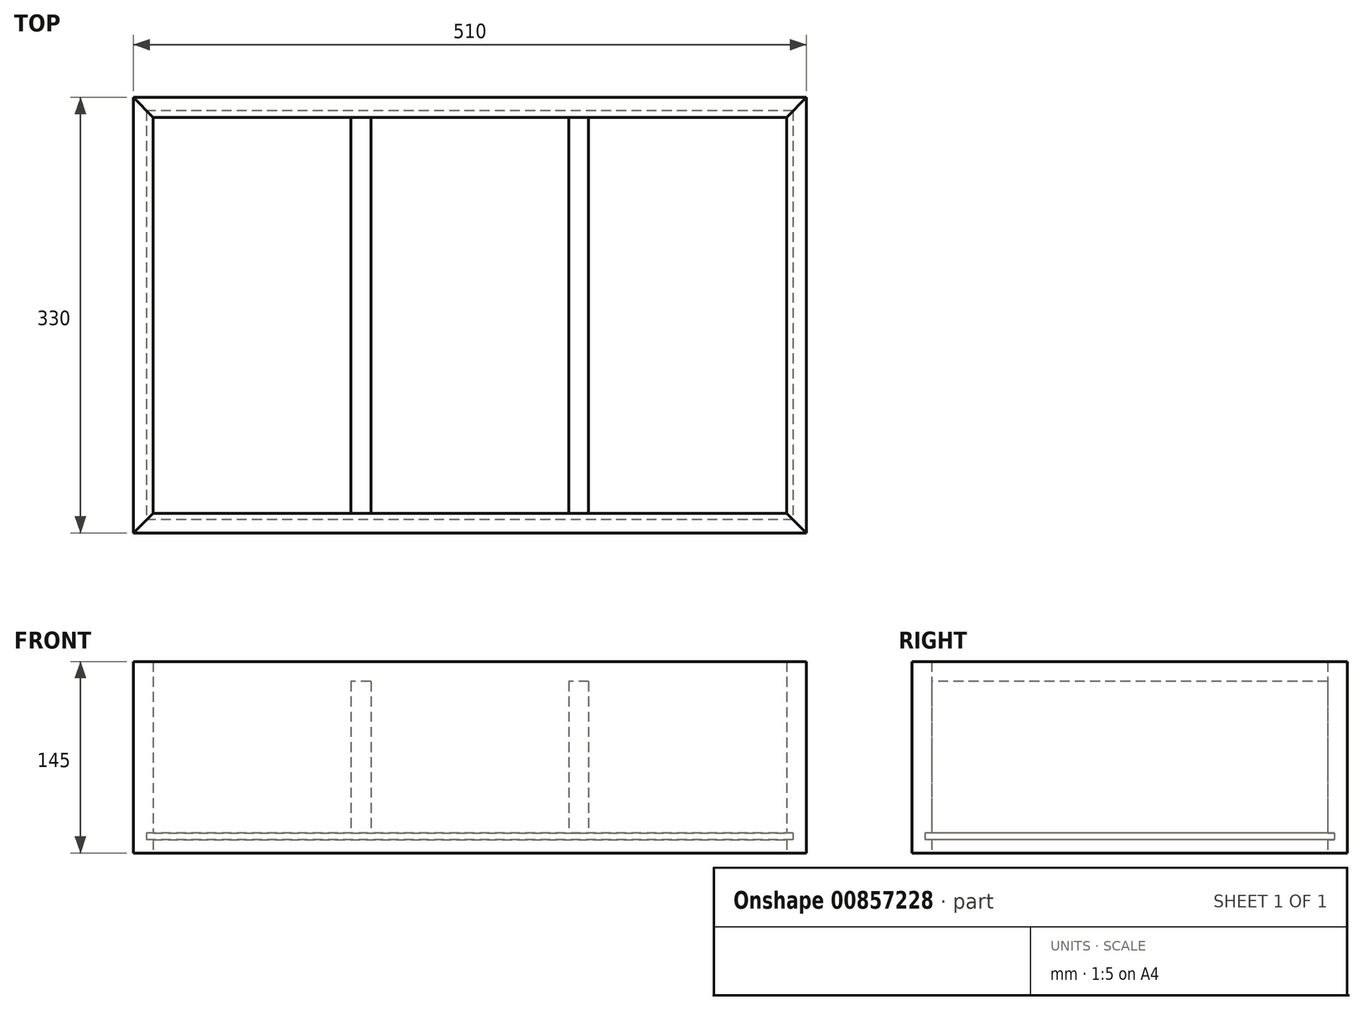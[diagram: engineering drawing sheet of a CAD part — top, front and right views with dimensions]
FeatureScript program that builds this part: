
annotation { "Feature Type Name" : "Feature", "Feature Type Description" : "" }
export const myFeature = defineFeature(function(context is Context, id is Id, definition is map)
    precondition{}
    {
        {
            var Q0;
            Q0=qCreatedBy(makeId("Front.planeOp"),FACE);
            var sketch = newSketch(context, id + "F0", { "sketchPlane" : qUnion([Q0])});
            skLineSegment(sketch, "E0", {"start": v(-255, 0) * mm, "end": v(255, 0) * mm, "construction": true});
            skLineSegment(sketch, "E1", {"start": v(255, 0) * mm, "end": v(255, 145) * mm, "construction": true});
            skLineSegment(sketch, "E2", {"start": v(255, 145) * mm, "end": v(-255, 145) * mm, "construction": true});
            skLineSegment(sketch, "E3", {"start": v(-255, 145) * mm, "end": v(-255, 0) * mm, "construction": true});
            skLineSegment(sketch, "E4", {"start": v(0, 145) * mm, "end": v(0, -38.8) * mm, "construction": true});
            skLineSegment(sketch, "E5", {"start": v(-255, 15) * mm, "end": v(255, 15) * mm, "construction": true});
            skLineSegment(sketch, "E6", {"start": v(-240, 145) * mm, "end": v(-240, 0) * mm, "construction": true});
            skLineSegment(sketch, "E7", {"start": v(-255, 130) * mm, "end": v(-240, 130) * mm, "construction": true});
            skLineSegment(sketch, "E8.MirrorCS", {"start": v(255, 130) * mm, "end": v(240, 130) * mm, "construction": true});
            skLineSegment(sketch, "E9.MirrorCS", {"start": v(240, 145) * mm, "end": v(240, 0) * mm, "construction": true});
            skLineSegment(sketch, "E10", {"start": v(-255, 10) * mm, "end": v(255, 10) * mm, "construction": true});
            skLineSegment(sketch, "E11", {"start": v(245, 15) * mm, "end": v(245, 10) * mm, "construction": true});
            skLineSegment(sketch, "E12.MirrorCS", {"start": v(-245, 15) * mm, "end": v(-245, 10) * mm, "construction": true});
            skLineSegment(sketch, "E13", {"start": v(-90, 15) * mm, "end": v(-90, 130) * mm, "construction": true});
            skLineSegment(sketch, "E14", {"start": v(-90, 130) * mm, "end": v(-75, 130) * mm, "construction": true});
            skLineSegment(sketch, "E15", {"start": v(-75, 130) * mm, "end": v(-75, 15) * mm, "construction": true});
            skLineSegment(sketch, "E16.MirrorCS", {"start": v(75, 130) * mm, "end": v(75, 15) * mm, "construction": true});
            skLineSegment(sketch, "E17.MirrorCS", {"start": v(90, 15) * mm, "end": v(90, 130) * mm, "construction": true});
            skLineSegment(sketch, "E18.MirrorCS", {"start": v(90, 130) * mm, "end": v(75, 130) * mm, "construction": true});
            skSolve(sketch);
        }
        {
            var Q0;
            Q0=qCreatedBy(makeId("Right.planeOp"),FACE);
            var sketch = newSketch(context, id + "F1", { "sketchPlane" : qUnion([Q0])});
            skLineSegment(sketch, "E19", {"start": v(0, 0) * mm, "end": v(330, 0) * mm, "construction": true});
            skLineSegment(sketch, "E20", {"start": v(330, 0) * mm, "end": v(330, 145) * mm, "construction": true});
            skLineSegment(sketch, "E21", {"start": v(330, 145) * mm, "end": v(0, 145) * mm, "construction": true});
            skLineSegment(sketch, "E22", {"start": v(0, 130) * mm, "end": v(330, 130) * mm, "construction": true});
            skLineSegment(sketch, "E23", {"start": v(165, 145) * mm, "end": v(165, 0) * mm, "construction": true});
            skLineSegment(sketch, "E24", {"start": v(315, 145) * mm, "end": v(315, 0) * mm, "construction": true});
            skLineSegment(sketch, "E25.MirrorCS", {"start": v(15, 145) * mm, "end": v(15, 0) * mm, "construction": true});
            skLineSegment(sketch, "E26", {"start": v(330, 15) * mm, "end": v(0, 15) * mm, "construction": true});
            skLineSegment(sketch, "E27", {"start": v(330, 10) * mm, "end": v(0, 10) * mm, "construction": true});
            skLineSegment(sketch, "E28", {"start": v(320, 15) * mm, "end": v(320, 10) * mm, "construction": true});
            skLineSegment(sketch, "E29.MirrorCS", {"start": v(10, 15) * mm, "end": v(10, 10) * mm, "construction": true});
            skSolve(sketch);
        }
        {
            var Q0;
            Q0=qCreatedBy(makeId("Top.planeOp"),FACE);
            var Q1;
            Q1=sQuery(id+"F1.wireOp",VERTEX,"E28.end");
            cPlane(context, id + "F2", {"entities" : qUnion([Q0, Q1]), "cplaneType" : CPlaneType.PLANE_POINT, "offset" : 25 * mm, "width" : 150 * mm, "height" : 150 * mm});
        }
        {
            var Q0;
            Q0=qCreatedBy(id+"F2.planeOp",FACE);
            var sketch = newSketch(context, id + "F3", { "sketchPlane" : qUnion([Q0])});
            skLineSegment(sketch, "E30.bottom", {"start": v(245, 320) * mm, "end": v(-245, 320) * mm});
            skLineSegment(sketch, "E30.top", {"start": v(245, 10) * mm, "end": v(-245, 10) * mm});
            skLineSegment(sketch, "E30.left", {"start": v(245, 320) * mm, "end": v(245, 10) * mm});
            skLineSegment(sketch, "E30.right", {"start": v(-245, 320) * mm, "end": v(-245, 10) * mm});
            skSolve(sketch);
        }
        {
            var Q0;
            Q0=qSketchRegion(id+"F3",true);
            var Q1;
            Q1=sQuery(id+"F1.wireOp",VERTEX,"E26.end");
            extrude(context, id + "F4", {"entities" : qUnion([Q0]), "endBound" : BoundingType.UP_TO_VERTEX, "depth" : 25 * mm, "endBoundEntityVertex" : qUnion([Q1]), "offsetDistance" : 25 * mm});
        }
        {
            var Q0;
            Q0=qCreatedBy(makeId("Top.planeOp"),FACE);
            var sketch = newSketch(context, id + "F5", { "sketchPlane" : qUnion([Q0])});
            skLineSegment(sketch, "E31", {"start": v(-240, 15) * mm, "end": v(-255, 0) * mm});
            skLineSegment(sketch, "E32", {"start": v(-240, 15) * mm, "end": v(240, 15) * mm});
            skLineSegment(sketch, "E33", {"start": v(255, 0) * mm, "end": v(240, 15) * mm});
            skLineSegment(sketch, "E34", {"start": v(255, 0) * mm, "end": v(-255, 0) * mm});
            skLineSegment(sketch, "E35", {"start": v(-225.32, 165) * mm, "end": v(297.83, 165) * mm, "construction": true});
            skLineSegment(sketch, "E36.MirrorCS", {"start": v(-240, 315) * mm, "end": v(240, 315) * mm});
            skLineSegment(sketch, "E37.MirrorCS", {"start": v(255, 330) * mm, "end": v(240, 315) * mm});
            skLineSegment(sketch, "E38.MirrorCS", {"start": v(255, 330) * mm, "end": v(-255, 330) * mm});
            skLineSegment(sketch, "E39.MirrorCS", {"start": v(-240, 315) * mm, "end": v(-255, 330) * mm});
            skLineSegment(sketch, "E40", {"start": v(-255, 0) * mm, "end": v(-255, 330) * mm});
            skLineSegment(sketch, "E41", {"start": v(-240, 315) * mm, "end": v(-240, 15) * mm});
            skLineSegment(sketch, "E42", {"start": v(255, 330) * mm, "end": v(255, 0) * mm});
            skLineSegment(sketch, "E43", {"start": v(240, 15) * mm, "end": v(240, 315) * mm});
            skSolve(sketch);
        }
        {
            var Q0;
            Q0=makeQuery(id+"F5.imprint","IMPRINT",FACE,{"disambiguationData":[TD([[makeQuery(id+"F5.imprint","IMPRINT",EDGE,{"derivedFrom":sQuery(id+"F5.wireOp",EDGE,"E31")}),1.0]])]});
            var Q1;
            Q1=makeQuery(id+"F5.imprint","IMPRINT",FACE,{"disambiguationData":[TD([[makeQuery(id+"F5.imprint","IMPRINT",EDGE,{"derivedFrom":sQuery(id+"F5.wireOp",EDGE,"E36.MirrorCS")}),1.0]])]});
            var Q2;
            Q2=sQuery(id+"F0.wireOp",VERTEX,"E4.start");
            extrude(context, id + "F6", {"entities" : qUnion([Q0, Q1]), "endBound" : BoundingType.UP_TO_VERTEX, "depth" : 25 * mm, "endBoundEntityVertex" : qUnion([Q2]), "offsetDistance" : 25 * mm});
        }
        {
            var Q0;
            Q0=makeQuery(id+"F5.imprint","IMPRINT",FACE,{"disambiguationData":[TD([[makeQuery(id+"F5.imprint","IMPRINT",EDGE,{"derivedFrom":sQuery(id+"F5.wireOp",EDGE,"E31")}),-1.0]])]});
            var Q1;
            Q1=makeQuery(id+"F5.imprint","IMPRINT",FACE,{"disambiguationData":[TD([[makeQuery(id+"F5.imprint","IMPRINT",EDGE,{"derivedFrom":sQuery(id+"F5.wireOp",EDGE,"E33")}),-1.0]])]});
            var Q2;
            Q2=makeQuery(id+"F6.opExtrude","CAP_FACE",FACE,{"disambiguationData":[OSD([sQuery(id+"F5.wireOp",EDGE,"E36.MirrorCS"),sQuery(id+"F5.wireOp",EDGE,"E37.MirrorCS"),sQuery(id+"F5.wireOp",EDGE,"E38.MirrorCS"),sQuery(id+"F5.wireOp",EDGE,"E39.MirrorCS")])],"isStart":false});
            extrude(context, id + "F7", {"entities" : qUnion([Q0, Q1]), "endBound" : BoundingType.UP_TO_SURFACE, "depth" : 25 * mm, "endBoundEntityFace" : qUnion([Q2]), "offsetDistance" : 25 * mm});
        }
        {
            var Q0;
            Q0=makeQuery(id+"F4.opExtrude","SWEPT_BODY",BODY,{"disambiguationData":[OSD([sQuery(id+"F3.wireOp",EDGE,"E30.bottom"),sQuery(id+"F3.wireOp",EDGE,"E30.top"),sQuery(id+"F3.wireOp",EDGE,"E30.left"),sQuery(id+"F3.wireOp",EDGE,"E30.right")])]});
            var Q1;
            {Q1=qUnion([makeQuery(id+"F6.opExtrude","SWEPT_BODY",BODY,{"disambiguationData":[OSD([sQuery(id+"F5.wireOp",EDGE,"E31"),sQuery(id+"F5.wireOp",EDGE,"E32"),sQuery(id+"F5.wireOp",EDGE,"E33"),sQuery(id+"F5.wireOp",EDGE,"E34")])]}),makeQuery(id+"F6.opExtrude","SWEPT_BODY",BODY,{"disambiguationData":[OSD([sQuery(id+"F5.wireOp",EDGE,"E36.MirrorCS"),sQuery(id+"F5.wireOp",EDGE,"E37.MirrorCS"),sQuery(id+"F5.wireOp",EDGE,"E38.MirrorCS"),sQuery(id+"F5.wireOp",EDGE,"E39.MirrorCS")])]})]);}
            var Q2;
            {Q2=qUnion([makeQuery(id+"F6.opExtrude","SWEPT_BODY",BODY,{"disambiguationData":[OSD([sQuery(id+"F5.wireOp",EDGE,"E31"),sQuery(id+"F5.wireOp",EDGE,"E32"),sQuery(id+"F5.wireOp",EDGE,"E33"),sQuery(id+"F5.wireOp",EDGE,"E34")])]}),makeQuery(id+"F6.opExtrude","SWEPT_BODY",BODY,{"disambiguationData":[OSD([sQuery(id+"F5.wireOp",EDGE,"E36.MirrorCS"),sQuery(id+"F5.wireOp",EDGE,"E37.MirrorCS"),sQuery(id+"F5.wireOp",EDGE,"E38.MirrorCS"),sQuery(id+"F5.wireOp",EDGE,"E39.MirrorCS")])]})]);}
            booleanBodies(context, id + "F8", {"operationType" : BooleanOperationType.SUBTRACTION, "tools" : qUnion([Q0]), "targets" : qUnion([Q1, Q2]), "oppositeDirection" : true, "keepTools" : true});
        }
        {
            var Q0;
            Q0=makeQuery(id+"F4.opExtrude","SWEPT_BODY",BODY,{"disambiguationData":[OSD([sQuery(id+"F3.wireOp",EDGE,"E30.bottom"),sQuery(id+"F3.wireOp",EDGE,"E30.top"),sQuery(id+"F3.wireOp",EDGE,"E30.left"),sQuery(id+"F3.wireOp",EDGE,"E30.right")])]});
            var Q1;
            {Q1=qUnion([makeQuery(id+"F7.opExtrude","SWEPT_BODY",BODY,{"disambiguationData":[OSD([sQuery(id+"F5.wireOp",EDGE,"E31"),sQuery(id+"F5.wireOp",EDGE,"E39.MirrorCS"),sQuery(id+"F5.wireOp",EDGE,"E40"),sQuery(id+"F5.wireOp",EDGE,"E41")])]}),makeQuery(id+"F7.opExtrude","SWEPT_BODY",BODY,{"disambiguationData":[OSD([sQuery(id+"F5.wireOp",EDGE,"E33"),sQuery(id+"F5.wireOp",EDGE,"E37.MirrorCS"),sQuery(id+"F5.wireOp",EDGE,"E42"),sQuery(id+"F5.wireOp",EDGE,"E43")])]})]);}
            var Q2;
            {Q2=qUnion([makeQuery(id+"F7.opExtrude","SWEPT_BODY",BODY,{"disambiguationData":[OSD([sQuery(id+"F5.wireOp",EDGE,"E31"),sQuery(id+"F5.wireOp",EDGE,"E39.MirrorCS"),sQuery(id+"F5.wireOp",EDGE,"E40"),sQuery(id+"F5.wireOp",EDGE,"E41")])]}),makeQuery(id+"F7.opExtrude","SWEPT_BODY",BODY,{"disambiguationData":[OSD([sQuery(id+"F5.wireOp",EDGE,"E33"),sQuery(id+"F5.wireOp",EDGE,"E37.MirrorCS"),sQuery(id+"F5.wireOp",EDGE,"E42"),sQuery(id+"F5.wireOp",EDGE,"E43")])]})]);}
            booleanBodies(context, id + "F9", {"operationType" : BooleanOperationType.SUBTRACTION, "tools" : qUnion([Q0]), "targets" : qUnion([Q1, Q2]), "keepTools" : true});
        }
        {
            var Q0;
            {var subQ2=sQuery(id+"F5.wireOp",EDGE,"E32");Q0=makeQuery(id+"F8.opBoolean","SPLIT",FACE,{"disambiguationData":[TD([makeQuery(id+"F4.opExtrude","CAP_FACE",FACE,{"disambiguationData":[OSD([sQuery(id+"F3.wireOp",EDGE,"E30.bottom"),sQuery(id+"F3.wireOp",EDGE,"E30.top"),sQuery(id+"F3.wireOp",EDGE,"E30.left"),sQuery(id+"F3.wireOp",EDGE,"E30.right")])],"isStart":false})])],"derivedFrom":makeQuery(id+"F6.opExtrude","SWEPT_FACE",FACE,{"disambiguationData":[OSD([subQ2])]})});}
            var sketch = newSketch(context, id + "F10", { "sketchPlane" : qUnion([Q0])});
            skLineSegment(sketch, "E44.bottom", {"start": v(-90, 130) * mm, "end": v(-75, 130) * mm});
            skLineSegment(sketch, "E44.top", {"start": v(-90, 15) * mm, "end": v(-75, 15) * mm});
            skLineSegment(sketch, "E44.left", {"start": v(-90, 130) * mm, "end": v(-90, 15) * mm});
            skLineSegment(sketch, "E44.right", {"start": v(-75, 130) * mm, "end": v(-75, 15) * mm});
            skLineSegment(sketch, "E45.bottom", {"start": v(75, 130) * mm, "end": v(90, 130) * mm});
            skLineSegment(sketch, "E45.top", {"start": v(75, 15) * mm, "end": v(90, 15) * mm});
            skLineSegment(sketch, "E45.left", {"start": v(75, 130) * mm, "end": v(75, 15) * mm});
            skLineSegment(sketch, "E45.right", {"start": v(90, 130) * mm, "end": v(90, 15) * mm});
            skSolve(sketch);
        }
        {
            var Q0;
            Q0=makeQuery(id+"F10.imprint","IMPRINT",FACE,{"disambiguationData":[TD([[makeQuery(id+"F10.imprint","IMPRINT",EDGE,{"derivedFrom":sQuery(id+"F10.wireOp",EDGE,"E44.bottom")}),-1.0]])]});
            var Q1;
            Q1=makeQuery(id+"F10.imprint","IMPRINT",FACE,{"disambiguationData":[TD([[makeQuery(id+"F10.imprint","IMPRINT",EDGE,{"derivedFrom":sQuery(id+"F10.wireOp",EDGE,"E45.bottom")}),-1.0]])]});
            var Q2;
            Q2=makeQuery(id+"F6.opExtrude","SWEPT_BODY",BODY,{"disambiguationData":[OSD([sQuery(id+"F5.wireOp",EDGE,"E36.MirrorCS"),sQuery(id+"F5.wireOp",EDGE,"E37.MirrorCS"),sQuery(id+"F5.wireOp",EDGE,"E38.MirrorCS"),sQuery(id+"F5.wireOp",EDGE,"E39.MirrorCS")])]});
            extrude(context, id + "F11", {"entities" : qUnion([Q0, Q1]), "endBound" : BoundingType.UP_TO_BODY, "depth" : 25 * mm, "endBoundEntityBody" : qUnion([Q2]), "offsetDistance" : 25 * mm});
        }
    });
